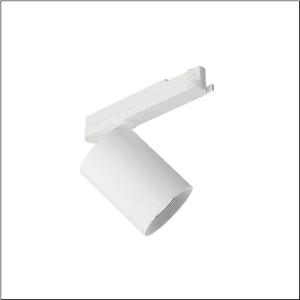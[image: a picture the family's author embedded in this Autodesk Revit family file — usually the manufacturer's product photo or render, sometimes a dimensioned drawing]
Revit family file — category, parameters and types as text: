
# Revit family: spot_21_51se13mba5b
name_source: partatom
category: Lighting Fixtures
units: mm (PartAtom-declared; Revit-internal decimal feet)

## family parameters
Cut with Voids When Loaded = No
Host = Face
Light Source = No
Part Type = Normal
Room Calculation Point = No
Round Connector Dimension = Use Diameter
Shared = No

## types (1)
- --- (1 x LED, 5300 lm, 41.8 W, 2700K)
    Apparent Load = 42 VA
    CIE Flux Codes = 95 98 99 100 100
    Color Rendering = 90
    Color Temperature = 2700K
    Default Elevation = 1800 mm
    Description = Spot 21, directional spotlight, light control with lens, of PMMA, LED rated luminous flux: 5.090lm, light colour: 927, control gear: ECG Multilumen, with 3-phase adapter, mains connection: 220..240V, AC, 50/60Hz, of aluminium, traffic white (RAL 9016), length: 213mm, diameter: 105mm, protection rating (complete): IP20, insulation class (complete): insulation class I (protective earthing), certification: CE, impact resistance: IK02, permissible ambient temperature for indoor applications: -20..+40°C, packaging unit: 1 piece
    Height = 175 mm
    Lamp = 1 x LED
    Lamp Light Flux = 5300 lm
    Lamp Power = 41.8 W
    Lamp count = 1
    Length = 105 mm
    Luminous efficacy = 127 lm/W
    Manufacturer = Siteco
    ModVariant = No
    Model = 51SE13MBA5B
    Mounting Place = Ceiling
    Mounting Type = Pendant
    Number of Poles = 1
    OnlyDefault = Yes
    Power Factor = 1
    Product Name = Spot 21
    Product group = directional spotlight
    ProductGroupID = 905
    Protection Class = Protection class I
    Protection Degree = IP 20
    RLX_Detail_Level = 1
    RLX_Emergency_Light_Flux = 0 lm
    RLX_Emergency_Type = 0
    RLX_Emergency_Type_DB = No
    RlxData = <blob elided: 17609 chars, md5=40f4bbb5>
    Socket = socket
    Standby Power = 0 W
    System Light Flux = 5300 lm
    System Power = 42 W
    Type Comments = factory setting: luminous flux: 100 % | (ON | ON | ON | ON) | 1050 mA
    Type Image = l_1003976.jpg
    URL = http://relux.com
    VarID = @adj_093713
    Voltage = 0 V
    Weight = 0.00 kg
    Width = 0 mm  [stored 0 ft]

note: [stored X ft] marks values corroborated as IEEE doubles in the binary element streams (Revit-internal decimal feet)

## geometry (parser evidence)
native form markers: Blend x4, Sweep x9
no freeform markers — native parametric forms only
